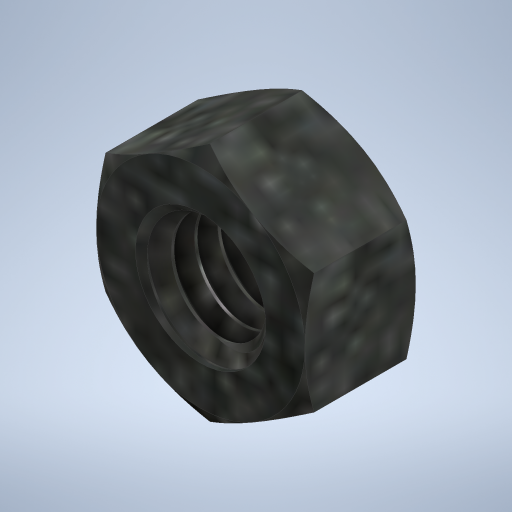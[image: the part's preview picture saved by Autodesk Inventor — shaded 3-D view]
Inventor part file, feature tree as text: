
AUTODESK INVENTOR PART (.ipt)
format: ipt  version: 2024 (Build 280153000, 153)  size: 505,344 bytes
history: native  units: in
note: dims shown in document units (in); Inventor stores cm internally (conversion verified against a paired STEP export)
features: mirror x1
ambient origin geometry x8: Origin, YZ Plane, XZ Plane, XY Plane, X Axis, Y Axis, Z Axis, Center Point
bodies: Solid1 (feature_tree)
feature tree (1):
  mirror  "Mirror1"
